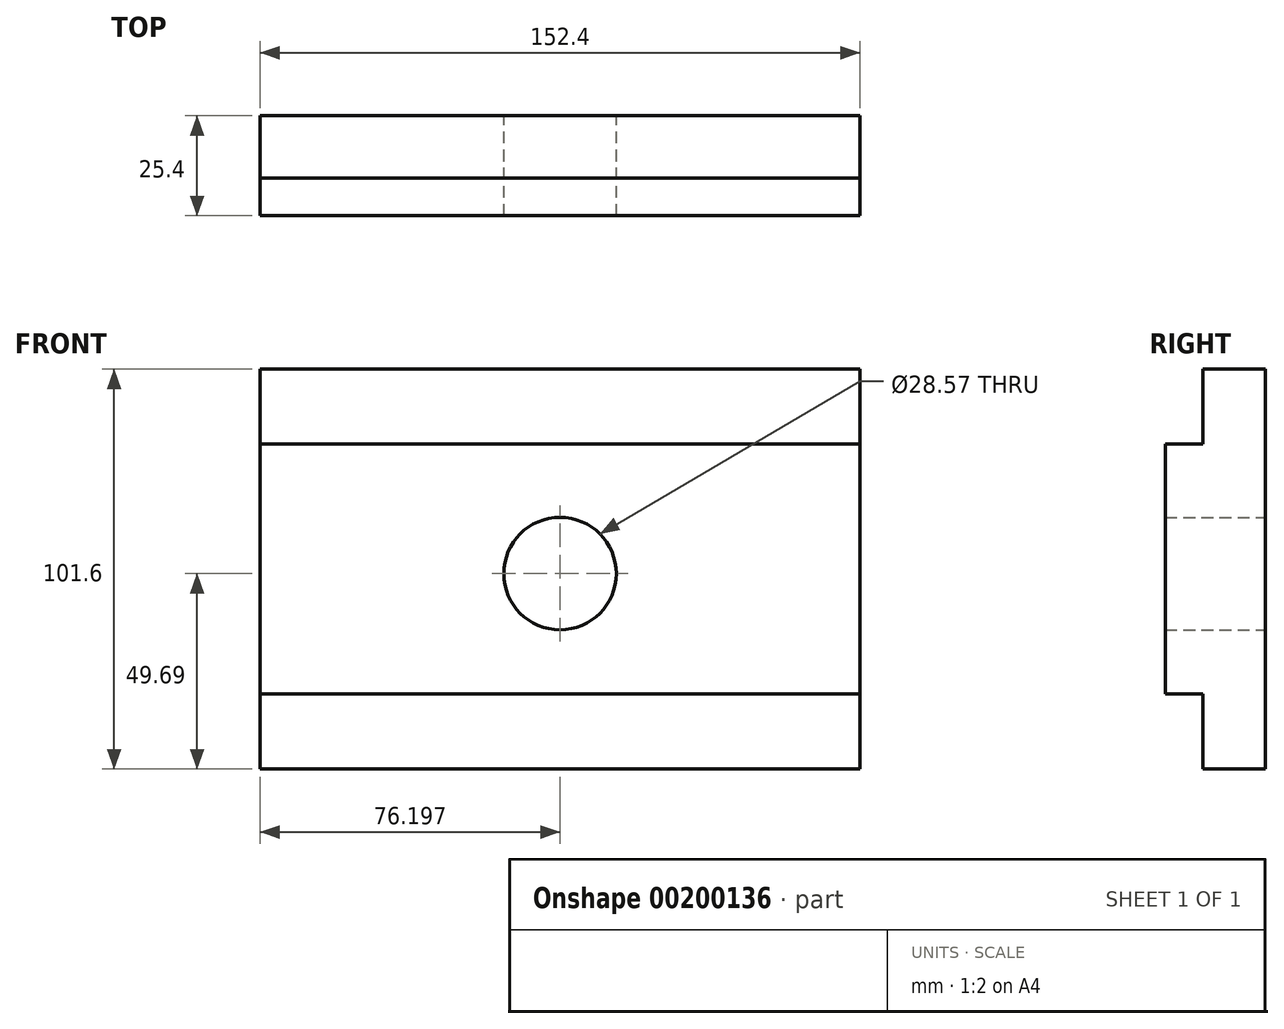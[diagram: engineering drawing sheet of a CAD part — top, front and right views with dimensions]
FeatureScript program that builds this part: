
annotation { "Feature Type Name" : "Feature", "Feature Type Description" : "" }
export const myFeature = defineFeature(function(context is Context, id is Id, definition is map)
    precondition{}
    {
        {
            var Q0;
            Q0=qCreatedBy(makeId("Front.planeOp"),FACE);
            var sketch = newSketch(context, id + "F0", { "sketchPlane" : qUnion([Q0])});
            skLineSegment(sketch, "E0.bottom", {"start": v(-85.75, 51.9) * mm, "end": v(66.65, 51.9) * mm});
            skLineSegment(sketch, "E0.top", {"start": v(-85.75, -49.7) * mm, "end": v(66.65, -49.7) * mm});
            skLineSegment(sketch, "E0.left", {"start": v(-85.75, 51.9) * mm, "end": v(-85.75, -49.7) * mm});
            skLineSegment(sketch, "E0.right", {"start": v(66.65, 51.9) * mm, "end": v(66.65, -49.7) * mm});
            skLineSegment(sketch, "E1", {"start": v(-85.75, 51.9) * mm, "end": v(-85.75, 32.86) * mm});
            skLineSegment(sketch, "E2", {"start": v(-85.75, -49.7) * mm, "end": v(-85.75, -30.64) * mm});
            skLineSegment(sketch, "E3.bottom", {"start": v(-85.75, 32.86) * mm, "end": v(66.65, 32.86) * mm});
            skLineSegment(sketch, "E3.top", {"start": v(-85.75, -30.64) * mm, "end": v(66.65, -30.64) * mm});
            skLineSegment(sketch, "E3.left", {"start": v(-85.75, 32.86) * mm, "end": v(-85.75, -30.64) * mm});
            skLineSegment(sketch, "E3.right", {"start": v(66.65, 32.86) * mm, "end": v(66.65, -30.64) * mm});
            skLineSegment(sketch, "E4", {"start": v(66.65, -49.7) * mm, "end": v(66.65, 0) * mm});
            skLineSegment(sketch, "E5", {"start": v(66.65, 51.9) * mm, "end": v(-9.55, 51.9) * mm});
            skPoint(sketch, "E6", {"position": v(-9.55, 0) * mm});
            skPoint(sketch, "E6.positionSnap0", {"position": v(-9.55, 32.86) * mm});
            skCircle(sketch, "E7", {"center": v(-9.55, 0) * mm, "radius": 14.29 * mm});
            skSolve(sketch);
        }
        {
            var Q0;
            Q0 = qSketchRegion(id + "F0", true);
            extrude(context, id + "F1", {"entities" : qUnion([Q0]), "depth" : 15.88 * mm});
        }
        {
            var Q0;
            Q0=makeQuery(id+"F0.imprint","IMPRINT",FACE,{"disambiguationData":[TD([[makeQuery(id+"F0.imprint","IMPRINT",EDGE,{"derivedFrom":sQuery(id+"F0.wireOp",EDGE,"E3.bottom")}),-1.0]])]});
            extrude(context, id + "F2", {"entities" : qUnion([Q0]), "operationType" : NewBodyOperationType.ADD, "depth" : 25.4 * mm});
        }
    });
